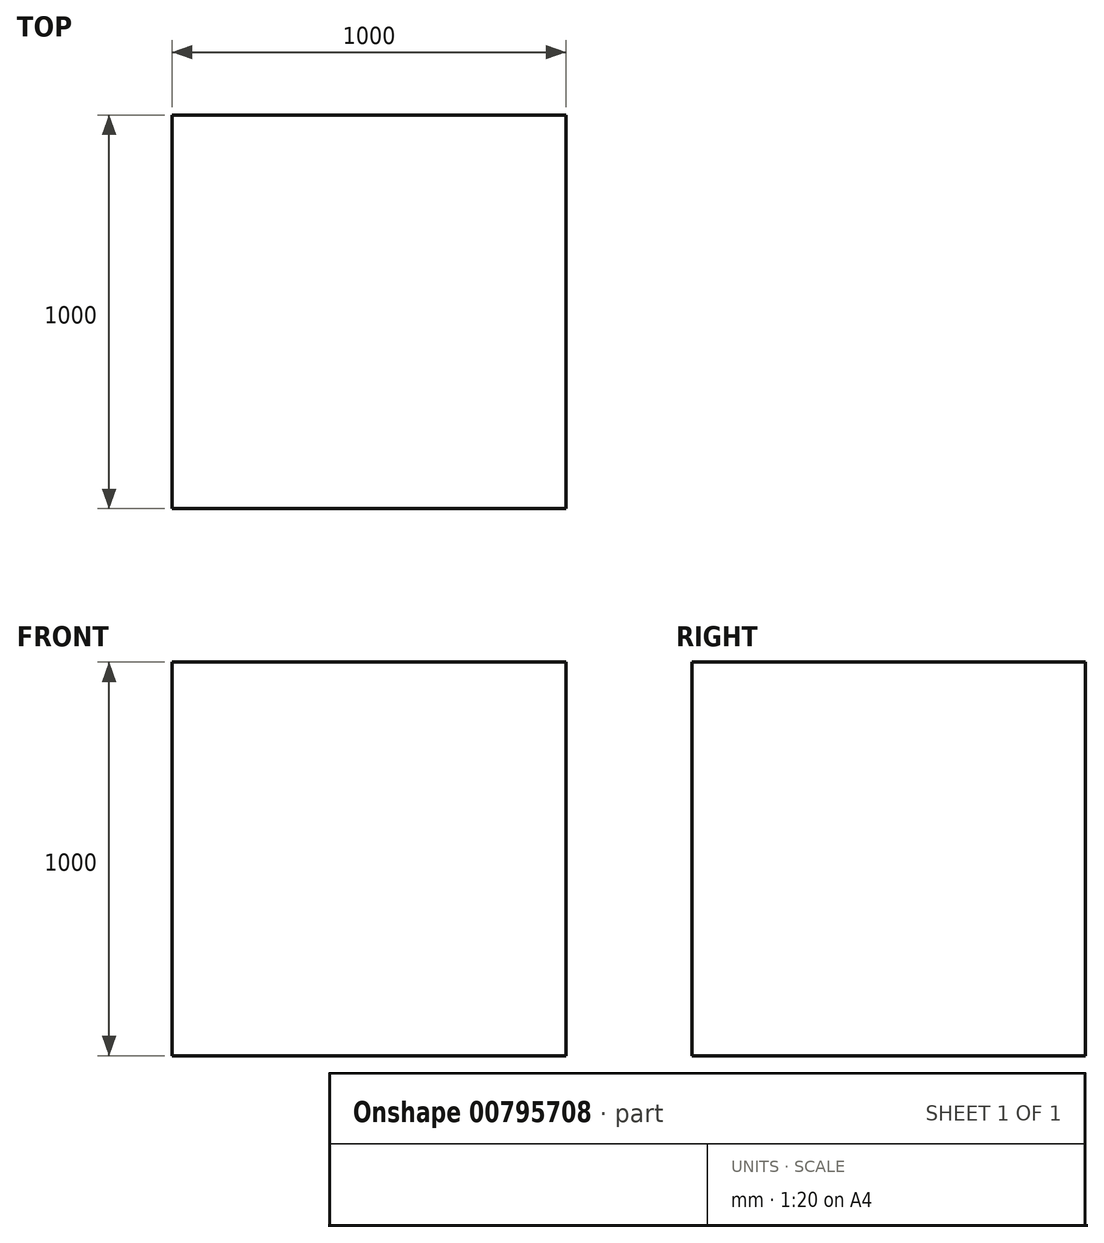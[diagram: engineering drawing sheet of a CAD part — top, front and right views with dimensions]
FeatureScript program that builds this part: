
annotation { "Feature Type Name" : "Feature", "Feature Type Description" : "" }
export const myFeature = defineFeature(function(context is Context, id is Id, definition is map)
    precondition{}
    {
        {
            var Q0;
            Q0=qCreatedBy(makeId("Front.planeOp"),FACE);
            var sketch = newSketch(context, id + "F0", { "sketchPlane" : qUnion([Q0])});
            skLineSegment(sketch, "E0", {"start": v(0, 0) * mm, "end": v(1000, 0) * mm});
            skSolve(sketch);
        }
        {
            var Q0;
            Q0=sQuery(id+"F0.wireOp",EDGE,"E0");
            extrude(context, id + "F1", {"bodyType" : ToolBodyType.SURFACE, "surfaceEntities" : qUnion([Q0]), "oppositeDirection" : true, "depth" : 1000 * mm, "offsetDistance" : 25 * mm});
        }
        {
            var Q0;
            Q0 = qSketchRegion(id + "F0", true);
            var Q1;
            Q1=makeQuery(id+"F1.opExtrude","SWEPT_FACE",FACE,{"disambiguationData":[OSD([sQuery(id+"F0.wireOp",EDGE,"E0")])]});
            extrude(context, id + "F2", {"entities" : qUnion([Q0, Q1]), "depth" : 1000 * mm, "offsetDistance" : 25 * mm});
        }
    });
